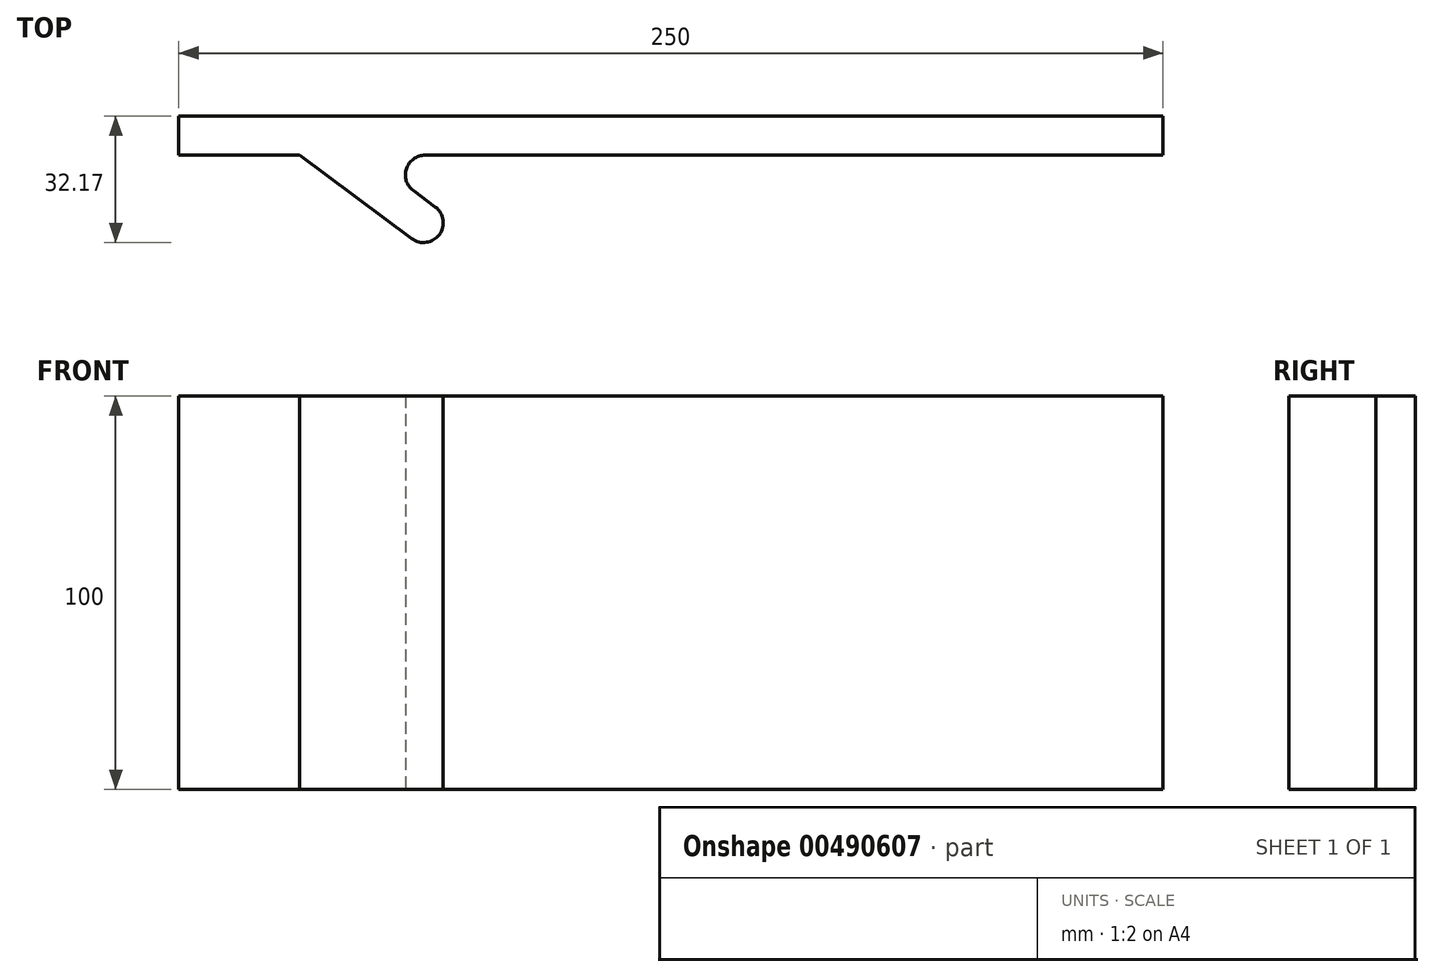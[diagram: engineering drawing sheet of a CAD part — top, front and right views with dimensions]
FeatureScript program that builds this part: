
annotation { "Feature Type Name" : "Feature", "Feature Type Description" : "" }
export const myFeature = defineFeature(function(context is Context, id is Id, definition is map)
    precondition{}
    {
        {
            var Q0;
            Q0=qCreatedBy(makeId("Front.planeOp"),FACE);
            var sketch = newSketch(context, id + "F0", { "sketchPlane" : qUnion([Q0])});
            skLineSegment(sketch, "E0.bottom", {"start": v(-125, 50) * mm, "end": v(125, 50) * mm});
            skLineSegment(sketch, "E0.top", {"start": v(-125, -50) * mm, "end": v(125, -50) * mm});
            skLineSegment(sketch, "E0.left", {"start": v(-125, 50) * mm, "end": v(-125, -50) * mm});
            skLineSegment(sketch, "E0.right", {"start": v(125, 50) * mm, "end": v(125, -50) * mm});
            skPoint(sketch, "E0.middle", {"position": v(0, 0) * mm});
            skSolve(sketch);
        }
        {
            var Q0;
            Q0=makeQuery(id+"F0.imprint","IMPRINT",FACE,{"disambiguationData":[TD([[makeQuery(id+"F0.imprint","IMPRINT",EDGE,{"derivedFrom":sQuery(id+"F0.wireOp",EDGE,"E0.bottom")}),-1.0]])]});
            extrude(context, id + "F1", {"entities" : qUnion([Q0]), "endBound" : BoundingType.SYMMETRIC, "depth" : 10 * mm});
        }
        {
            var Q0;
            Q0=qCreatedBy(makeId("Right.planeOp"),FACE);
            cPlane(context, id + "F2", {"entities" : qUnion([Q0]), "cplaneType" : CPlaneType.OFFSET, "offset" : 195 * mm, "oppositeDirection" : true, "width" : 150 * mm, "height" : 150 * mm});
        }
        {
            var Q0;
            Q0=qCreatedBy(makeId("Top.planeOp"),FACE);
            var sketch = newSketch(context, id + "F3", { "sketchPlane" : qUnion([Q0])});
            skLineSegment(sketch, "E1.bottom", {"start": v(125, -5) * mm, "end": v(-125, -5) * mm});
            skLineSegment(sketch, "E1.top", {"start": v(125, 5) * mm, "end": v(-125, 5) * mm});
            skLineSegment(sketch, "E1.left", {"start": v(125, -5) * mm, "end": v(125, 5) * mm});
            skLineSegment(sketch, "E1.right", {"start": v(-125, -5) * mm, "end": v(-125, 5) * mm});
            skPoint(sketch, "E1.middle", {"position": v(0, 0) * mm});
            skLineSegment(sketch, "E2", {"start": v(-94.35, -5) * mm, "end": v(-61.78, -29.16) * mm});
            skLineSegment(sketch, "E3", {"start": v(-61.78, -29.16) * mm, "end": v(-55.82, -21.13) * mm});
            skLineSegment(sketch, "E4", {"start": v(-55.82, -21.13) * mm, "end": v(-77.57, -5) * mm});
            skLineSegment(sketch, "E5", {"start": v(-77.57, -5) * mm, "end": v(-94.35, -5) * mm});
            skSolve(sketch);
        }
        {
            var Q0;
            Q0=makeQuery(id+"F3.imprint","IMPRINT",FACE,{"disambiguationData":[TD([[makeQuery(id+"F3.imprint","IMPRINT",EDGE,{"derivedFrom":sQuery(id+"F3.wireOp",EDGE,"E2")}),1.0]])]});
            extrude(context, id + "F4", {"entities" : qUnion([Q0]), "operationType" : NewBodyOperationType.ADD, "endBound" : BoundingType.SYMMETRIC, "depth" : 100 * mm});
        }
        {
            var Q0;
            Q0=makeQuery(id+"F4.opExtrude","SWEPT_EDGE",EDGE,{"disambiguationData":[OSD([sQuery(id+"F3.wireOp",EDGE,"E1.bottom"),sQuery(id+"F3.wireOp",EDGE,"E2"),sQuery(id+"F3.wireOp",EDGE,"E5")])]});
            var Q1;
            Q1=makeQuery(id+"F4.opExtrude","SWEPT_EDGE",EDGE,{"disambiguationData":[OSD([sQuery(id+"F3.wireOp",EDGE,"E1.bottom"),sQuery(id+"F3.wireOp",EDGE,"E4"),sQuery(id+"F3.wireOp",EDGE,"E5")])]});
            fillet(context, id + "F5", {"entities" : qUnion([Q0, Q1]), "radius" : 5 * mm, "tangentPropagation" : true, "allowEdgeOverflow" : false});
        }
        {
            var Q0;
            Q0=makeQuery(id+"F5.opFillet","BLEND_EDGE",EDGE,{"blendedFrom":[makeQuery(id+"F4.opExtrude","SWEPT_EDGE",EDGE,{"disambiguationData":[OSD([sQuery(id+"F3.wireOp",EDGE,"E1.bottom"),sQuery(id+"F3.wireOp",EDGE,"E4"),sQuery(id+"F3.wireOp",EDGE,"E5")])]}),makeQuery(id+"F4.opExtrude","SWEPT_FACE",FACE,{"disambiguationData":[OSD([sQuery(id+"F3.wireOp",EDGE,"E3")])]})],"blendedInto":[makeQuery(id+"F4.opExtrude","SWEPT_FACE",FACE,{"disambiguationData":[OSD([sQuery(id+"F3.wireOp",EDGE,"E3")])]})]});
            var Q1;
            Q1=makeQuery(id+"F4.opExtrude","SWEPT_EDGE",EDGE,{"disambiguationData":[OSD([sQuery(id+"F3.wireOp",EDGE,"E2"),sQuery(id+"F3.wireOp",EDGE,"E3")])]});
            fillet(context, id + "F6", {"entities" : qUnion([Q0, Q1]), "radius" : 5 * mm, "tangentPropagation" : true, "allowEdgeOverflow" : false});
        }
        {
            var Q0;
            Q0=makeQuery(id+"F4.opExtrude","SWEPT_EDGE",EDGE,{"disambiguationData":[OSD([sQuery(id+"F3.wireOp",EDGE,"E3"),sQuery(id+"F3.wireOp",EDGE,"E4")])]});
            fillet(context, id + "F7", {"entities" : qUnion([Q0]), "radius" : 5 * mm, "tangentPropagation" : true, "allowEdgeOverflow" : false});
        }
    });
